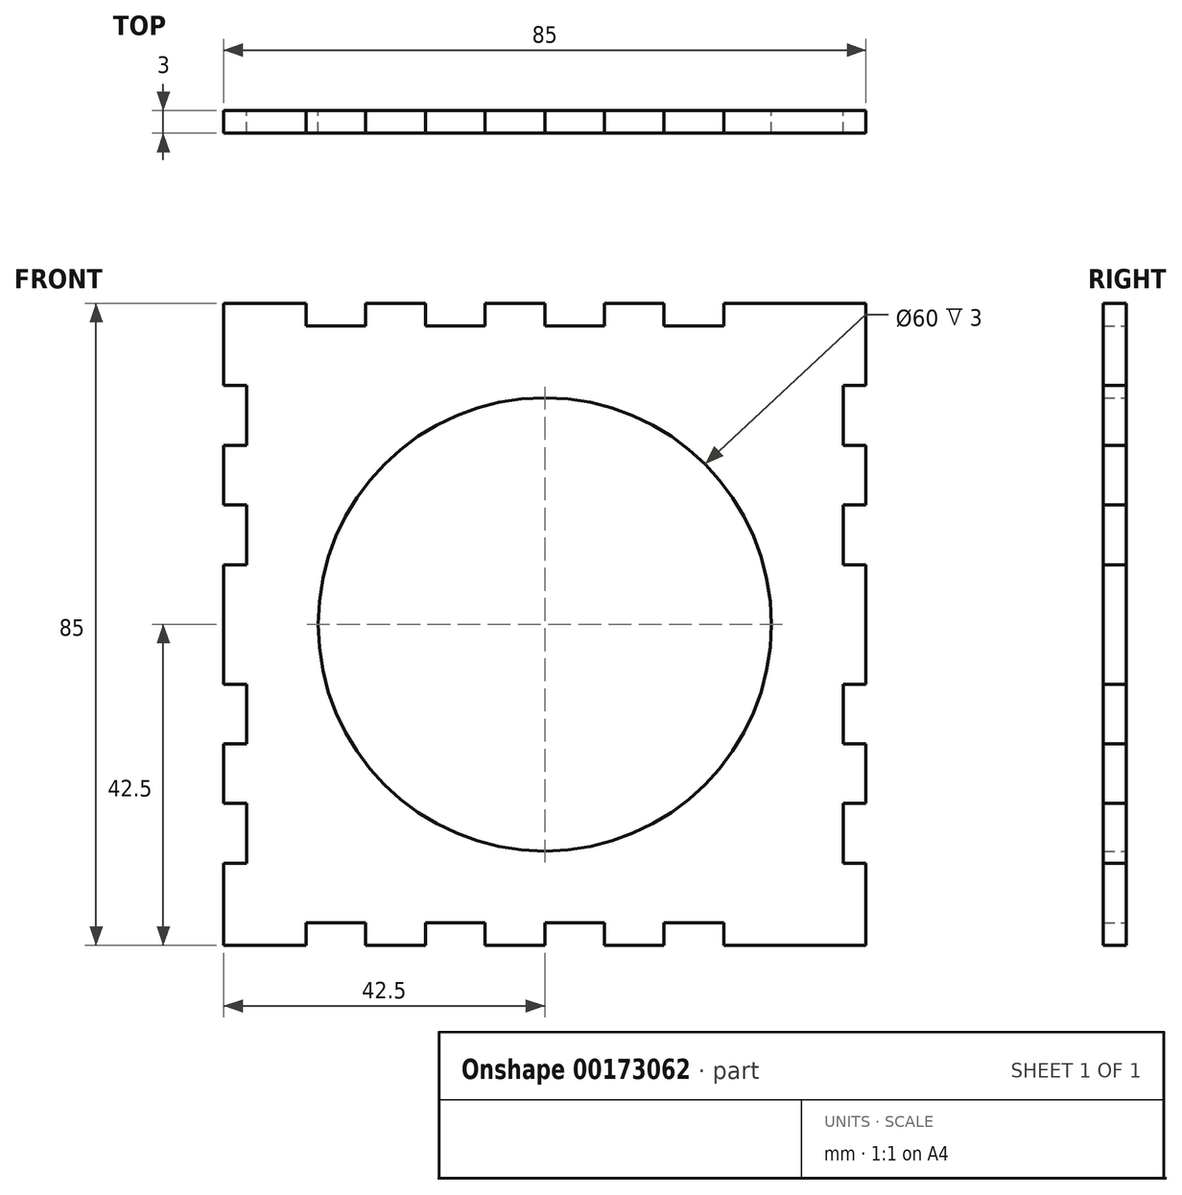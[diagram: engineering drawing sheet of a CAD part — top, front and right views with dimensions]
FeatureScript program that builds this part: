
annotation { "Feature Type Name" : "Feature", "Feature Type Description" : "" }
export const myFeature = defineFeature(function(context is Context, id is Id, definition is map)
    precondition{}
    {
        {
            var Q0;
            Q0=qCreatedBy(makeId("Front.planeOp"),FACE);
            var sketch = newSketch(context, id + "F0", { "sketchPlane" : qUnion([Q0])});
            skLineSegment(sketch, "E0.top", {"start": v(-42.5, -42.5) * mm, "end": v(-31.6, -42.5) * mm});
            skArc(sketch, "E1", {"start": v(0, 30) * mm, "mid": v(-30, 0) * mm, "end": v(0, -30) * mm});
            skLineSegment(sketch, "E2", {"start": v(-42.5, 0) * mm, "end": v(-39.5, 0) * mm});
            skLineSegment(sketch, "E3", {"start": v(-39.5, -7.9) * mm, "end": v(-42.5, -7.9) * mm});
            skLineSegment(sketch, "E4", {"start": v(-42.5, -15.8) * mm, "end": v(-39.5, -15.8) * mm});
            skLineSegment(sketch, "E5", {"start": v(-42.5, -23.7) * mm, "end": v(-39.5, -23.7) * mm});
            skLineSegment(sketch, "E6", {"start": v(-42.5, -31.6) * mm, "end": v(-39.5, -31.6) * mm});
            skLineSegment(sketch, "E7.trimOffspring", {"start": v(-42.5, 0) * mm, "end": v(-42.5, -7.9) * mm});
            skLineSegment(sketch, "E8.trimOffspring", {"start": v(-42.5, -15.8) * mm, "end": v(-42.5, -23.7) * mm});
            skLineSegment(sketch, "E9.trimOffspring", {"start": v(-42.5, -31.6) * mm, "end": v(-42.5, -42.5) * mm});
            skPoint(sketch, "E0.right.start.orphan", {"position": v(42.5, 42.5) * mm});
            skPoint(sketch, "E10.orphan", {"position": v(42.5, -42.5) * mm});
            skLineSegment(sketch, "E11.MirrorCS", {"start": v(42.5, -31.6) * mm, "end": v(39.5, -31.6) * mm});
            skLineSegment(sketch, "E12.MirrorCS", {"start": v(39.5, -7.9) * mm, "end": v(42.5, -7.9) * mm});
            skLineSegment(sketch, "E13.MirrorCS", {"start": v(42.5, 0) * mm, "end": v(39.5, 0) * mm});
            skLineSegment(sketch, "E14.MirrorCS", {"start": v(42.5, -15.8) * mm, "end": v(39.5, -15.8) * mm});
            skLineSegment(sketch, "E15.MirrorCS", {"start": v(42.5, -23.7) * mm, "end": v(39.5, -23.7) * mm});
            skLineSegment(sketch, "E16.MirrorCS", {"start": v(42.5, -31.6) * mm, "end": v(42.5, -42.5) * mm});
            skLineSegment(sketch, "E17.MirrorCS", {"start": v(42.5, -15.8) * mm, "end": v(42.5, -23.7) * mm});
            skLineSegment(sketch, "E18.MirrorCS", {"start": v(42.5, 0) * mm, "end": v(42.5, -7.9) * mm});
            skLineSegment(sketch, "E19.MirrorCS", {"start": v(42.5, -42.5) * mm, "end": v(23.7, -42.5) * mm});
            skArc(sketch, "E20.MirrorCS", {"start": v(0, 30) * mm, "mid": v(30, 0) * mm, "end": v(0, -30) * mm});
            skLineSegment(sketch, "E21.trimOffspring", {"start": v(-39.5, -7.9) * mm, "end": v(-39.5, -15.8) * mm});
            skLineSegment(sketch, "E22.trimOffspring", {"start": v(-39.5, -23.7) * mm, "end": v(-39.5, -31.6) * mm});
            skLineSegment(sketch, "E23.trimOffspring", {"start": v(39.5, -23.7) * mm, "end": v(39.5, -31.6) * mm});
            skLineSegment(sketch, "E24.trimOffspring", {"start": v(39.5, -7.9) * mm, "end": v(39.5, -15.8) * mm});
            skLineSegment(sketch, "E25", {"start": v(-31.6, -39.5) * mm, "end": v(-31.6, -42.5) * mm});
            skLineSegment(sketch, "E26", {"start": v(-23.7, -39.5) * mm, "end": v(-23.7, -42.5) * mm});
            skLineSegment(sketch, "E27", {"start": v(-15.8, -39.5) * mm, "end": v(-15.8, -42.5) * mm});
            skLineSegment(sketch, "E28", {"start": v(-7.9, -39.5) * mm, "end": v(-7.9, -42.5) * mm});
            skLineSegment(sketch, "E29", {"start": v(0, -39.5) * mm, "end": v(0, -42.5) * mm});
            skLineSegment(sketch, "E30", {"start": v(7.9, -39.5) * mm, "end": v(7.9, -42.5) * mm});
            skLineSegment(sketch, "E31", {"start": v(15.8, -39.5) * mm, "end": v(15.8, -42.5) * mm});
            skLineSegment(sketch, "E32", {"start": v(23.7, -39.5) * mm, "end": v(23.7, -42.5) * mm});
            skLineSegment(sketch, "E33.trimOffspring", {"start": v(-23.7, -42.5) * mm, "end": v(-15.8, -42.5) * mm});
            skLineSegment(sketch, "E34.trimOffspring", {"start": v(-7.9, -42.5) * mm, "end": v(0, -42.5) * mm});
            skPoint(sketch, "E35.orphan", {"position": v(0, -42.5) * mm});
            skLineSegment(sketch, "E36.trimOffspring", {"start": v(15.8, -42.5) * mm, "end": v(7.9, -42.5) * mm});
            skPoint(sketch, "E37.end.orphan", {"position": v(31.6, -42.5) * mm});
            skPoint(sketch, "E37.start.orphan", {"position": v(31.6, -39.5) * mm});
            skLineSegment(sketch, "E38.trimOffspring", {"start": v(23.7, -39.5) * mm, "end": v(15.8, -39.5) * mm});
            skPoint(sketch, "E39.orphan", {"position": v(39.5, -39.5) * mm});
            skPoint(sketch, "E40.orphan", {"position": v(-39.5, -39.5) * mm});
            skPoint(sketch, "E41.MirrorCS.end.orphan", {"position": v(39.5, 7.9) * mm});
            skPoint(sketch, "E42.MirrorCS.end.orphan", {"position": v(42.5, 7.9) * mm});
            skPoint(sketch, "E43.MirrorCS.start.orphan", {"position": v(42.5, 15.8) * mm});
            skPoint(sketch, "E44.trimOffspring.end.orphan", {"position": v(39.5, 15.8) * mm});
            skPoint(sketch, "E45.MirrorCS.end.orphan", {"position": v(39.5, 23.7) * mm});
            skPoint(sketch, "E46.MirrorCS.end.orphan", {"position": v(42.5, 23.7) * mm});
            skPoint(sketch, "E47.MirrorCS.end.orphan", {"position": v(42.5, 31.6) * mm});
            skPoint(sketch, "E47.MirrorCS.start.orphan", {"position": v(39.5, 31.6) * mm});
            skPoint(sketch, "E48.MirrorCS.end.orphan", {"position": v(0, 39.5) * mm});
            skPoint(sketch, "E49.MirrorCS.end.orphan", {"position": v(0, 42.5) * mm});
            skPoint(sketch, "E50.MirrorCS.end.orphan", {"position": v(42.5, 39.5) * mm});
            skPoint(sketch, "E50.MirrorCS.start.orphan", {"position": v(39.5, 39.5) * mm});
            skPoint(sketch, "E0.left.start.orphan", {"position": v(-42.5, 42.5) * mm});
            skPoint(sketch, "E51.end.orphan", {"position": v(-42.5, 39.5) * mm});
            skPoint(sketch, "E52.left.start.orphan", {"position": v(-39.5, 39.5) * mm});
            skPoint(sketch, "E53.start.orphan", {"position": v(-39.5, 31.6) * mm});
            skPoint(sketch, "E54.trimOffspring.start.orphan", {"position": v(-42.5, 31.6) * mm});
            skPoint(sketch, "E55.start.orphan", {"position": v(-42.5, 23.7) * mm});
            skPoint(sketch, "E56.trimOffspring.start.orphan", {"position": v(-39.5, 23.7) * mm});
            skPoint(sketch, "E57.end.orphan", {"position": v(-39.5, 15.8) * mm});
            skPoint(sketch, "E58.trimOffspring.start.orphan", {"position": v(-42.5, 15.8) * mm});
            skPoint(sketch, "E59.start.orphan", {"position": v(-42.5, 7.9) * mm});
            skPoint(sketch, "E60.trimOffspring.start.orphan", {"position": v(-39.5, 7.9) * mm});
            skLineSegment(sketch, "E61.MirrorCS", {"start": v(0, 39.5) * mm, "end": v(0, 42.5) * mm});
            skLineSegment(sketch, "E62.MirrorCS", {"start": v(23.7, 39.5) * mm, "end": v(23.7, 42.5) * mm});
            skLineSegment(sketch, "E63.MirrorCS", {"start": v(-31.6, 39.5) * mm, "end": v(-31.6, 42.5) * mm});
            skLineSegment(sketch, "E64.MirrorCS", {"start": v(15.8, 39.5) * mm, "end": v(15.8, 42.5) * mm});
            skLineSegment(sketch, "E65.MirrorCS", {"start": v(-15.8, 39.5) * mm, "end": v(-15.8, 42.5) * mm});
            skLineSegment(sketch, "E66.MirrorCS", {"start": v(42.5, 23.7) * mm, "end": v(39.5, 23.7) * mm});
            skLineSegment(sketch, "E67.MirrorCS", {"start": v(-23.7, 39.5) * mm, "end": v(-23.7, 42.5) * mm});
            skLineSegment(sketch, "E68.MirrorCS", {"start": v(42.5, 31.6) * mm, "end": v(39.5, 31.6) * mm});
            skLineSegment(sketch, "E69.MirrorCS", {"start": v(39.5, 7.9) * mm, "end": v(42.5, 7.9) * mm});
            skLineSegment(sketch, "E70.MirrorCS", {"start": v(7.9, 39.5) * mm, "end": v(7.9, 42.5) * mm});
            skLineSegment(sketch, "E71.MirrorCS", {"start": v(-7.9, 39.5) * mm, "end": v(-7.9, 42.5) * mm});
            skLineSegment(sketch, "E72.MirrorCS", {"start": v(42.5, 15.8) * mm, "end": v(39.5, 15.8) * mm});
            skLineSegment(sketch, "E73.MirrorCS", {"start": v(-42.5, 31.6) * mm, "end": v(-39.5, 31.6) * mm});
            skLineSegment(sketch, "E74.MirrorCS", {"start": v(-42.5, 23.7) * mm, "end": v(-39.5, 23.7) * mm});
            skLineSegment(sketch, "E75.MirrorCS", {"start": v(-42.5, 15.8) * mm, "end": v(-39.5, 15.8) * mm});
            skLineSegment(sketch, "E76.MirrorCS", {"start": v(-39.5, 7.9) * mm, "end": v(-42.5, 7.9) * mm});
            skLineSegment(sketch, "E77.MirrorCS", {"start": v(42.5, 15.8) * mm, "end": v(42.5, 23.7) * mm});
            skLineSegment(sketch, "E78.MirrorCS", {"start": v(-39.5, 7.9) * mm, "end": v(-39.5, 15.8) * mm});
            skLineSegment(sketch, "E79.MirrorCS", {"start": v(-23.7, 42.5) * mm, "end": v(-15.8, 42.5) * mm});
            skPoint(sketch, "E80.MirrorP", {"position": v(31.6, 39.5) * mm});
            skLineSegment(sketch, "E81.MirrorCS", {"start": v(42.5, 0) * mm, "end": v(42.5, 7.9) * mm});
            skLineSegment(sketch, "E82.MirrorCS", {"start": v(42.5, 31.6) * mm, "end": v(42.5, 42.5) * mm});
            skLineSegment(sketch, "E83.MirrorCS", {"start": v(23.7, 39.5) * mm, "end": v(15.8, 39.5) * mm});
            skLineSegment(sketch, "E84.MirrorCS", {"start": v(15.8, 42.5) * mm, "end": v(7.9, 42.5) * mm});
            skLineSegment(sketch, "E85.MirrorCS", {"start": v(39.5, 23.7) * mm, "end": v(39.5, 31.6) * mm});
            skLineSegment(sketch, "E86.MirrorCS", {"start": v(-39.5, 23.7) * mm, "end": v(-39.5, 31.6) * mm});
            skPoint(sketch, "E87.MirrorP", {"position": v(31.6, 42.5) * mm});
            skLineSegment(sketch, "E88.MirrorCS", {"start": v(-42.5, 42.5) * mm, "end": v(-31.6, 42.5) * mm});
            skLineSegment(sketch, "E89.MirrorCS", {"start": v(39.5, 7.9) * mm, "end": v(39.5, 15.8) * mm});
            skLineSegment(sketch, "E90.MirrorCS", {"start": v(-7.9, 42.5) * mm, "end": v(0, 42.5) * mm});
            skLineSegment(sketch, "E91.MirrorCS", {"start": v(42.5, 42.5) * mm, "end": v(23.7, 42.5) * mm});
            skLineSegment(sketch, "E92.MirrorCS", {"start": v(-31.6, 39.5) * mm, "end": v(-23.7, 39.5) * mm});
            skLineSegment(sketch, "E93.MirrorCS", {"start": v(-42.5, 0) * mm, "end": v(-42.5, 7.9) * mm});
            skLineSegment(sketch, "E94.MirrorCS", {"start": v(-42.5, 31.6) * mm, "end": v(-42.5, 42.5) * mm});
            skLineSegment(sketch, "E95.MirrorCS", {"start": v(-42.5, 15.8) * mm, "end": v(-42.5, 23.7) * mm});
            skLineSegment(sketch, "E96.trimOffspring", {"start": v(-15.8, 39.5) * mm, "end": v(-7.9, 39.5) * mm});
            skLineSegment(sketch, "E97.trimOffspring", {"start": v(7.9, 39.5) * mm, "end": v(0, 39.5) * mm});
            skLineSegment(sketch, "E98.trimOffspring", {"start": v(-15.8, -39.5) * mm, "end": v(-7.9, -39.5) * mm});
            skLineSegment(sketch, "E99.trimOffspring", {"start": v(7.9, -39.5) * mm, "end": v(0, -39.5) * mm});
            skPoint(sketch, "E100.MirrorCS.start.orphan", {"position": v(0, 30) * mm});
            skPoint(sketch, "E101.orphan", {"position": v(0, -39.5) * mm});
            skLineSegment(sketch, "E102", {"start": v(-31.6, -39.5) * mm, "end": v(-23.7, -39.5) * mm});
            skSolve(sketch);
        }
        {
            var Q0;
            Q0=qSketchRegion(id+"F0",true);
            extrude(context, id + "F1", {"entities" : qUnion([Q0]), "depth" : 3 * mm});
        }
    });
